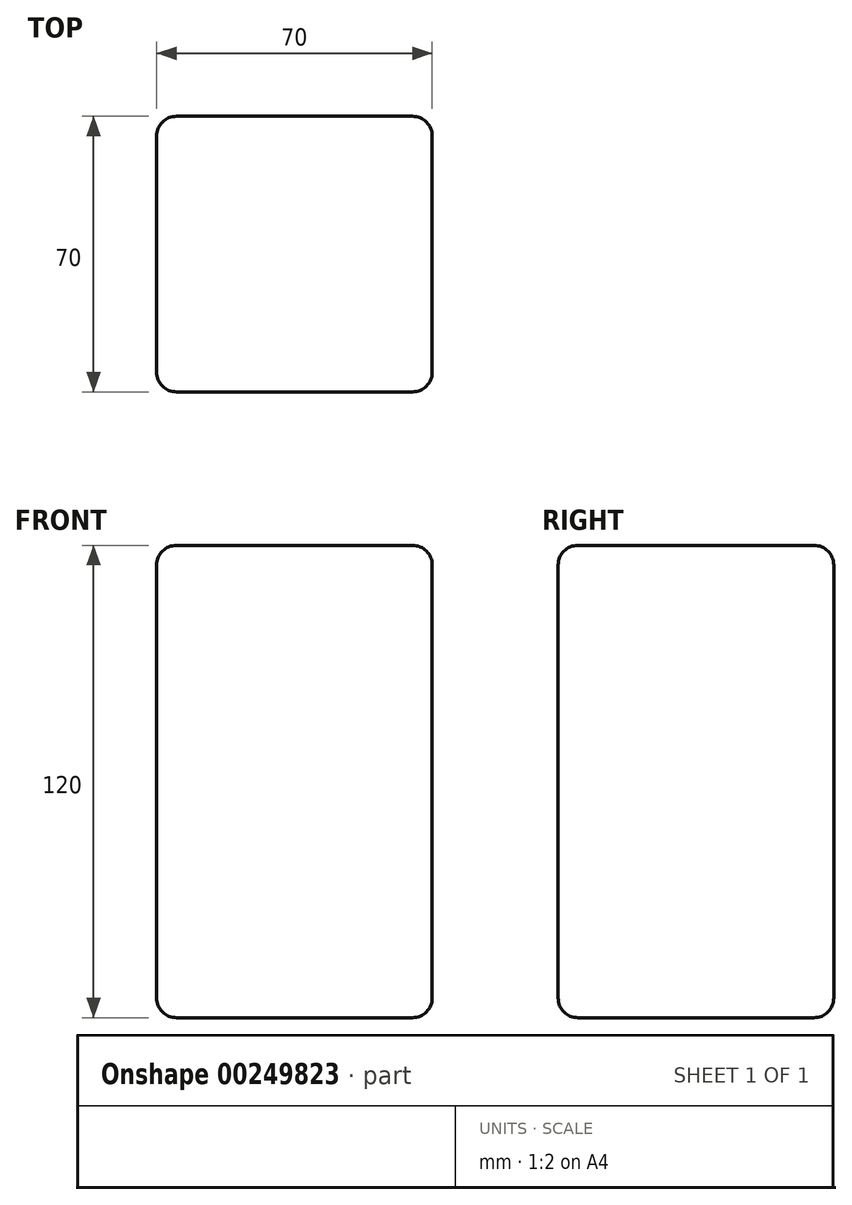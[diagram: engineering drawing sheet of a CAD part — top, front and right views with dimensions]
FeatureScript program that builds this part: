
annotation { "Feature Type Name" : "Feature", "Feature Type Description" : "" }
export const myFeature = defineFeature(function(context is Context, id is Id, definition is map)
    precondition{}
    {
        {
            var Q0;
            Q0=qCreatedBy(makeId("Top.planeOp"),FACE);
            var sketch = newSketch(context, id + "F0", { "sketchPlane" : qUnion([Q0])});
            skLineSegment(sketch, "E0.bottom", {"start": v(30, -34.82) * mm, "end": v(-30, -34.82) * mm});
            skLineSegment(sketch, "E0.top", {"start": v(30, 35.18) * mm, "end": v(-30, 35.18) * mm});
            skLineSegment(sketch, "E0.left", {"start": v(35, -29.82) * mm, "end": v(35, 30.18) * mm});
            skLineSegment(sketch, "E0.right", {"start": v(-35, -29.82) * mm, "end": v(-35, 30.18) * mm});
            skPoint(sketch, "E0.middle", {"position": v(0, 0.18) * mm});
            skPoint(sketch, "E1.visualSharp", {"position": v(-35, -34.82) * mm});
            skArc(sketch, "E1.filletArc", {"start": v(-35, -29.82) * mm, "mid": v(-33.54, -33.35) * mm, "end": v(-30, -34.82) * mm});
            skPoint(sketch, "E2.visualSharp", {"position": v(-35, 35.18) * mm});
            skArc(sketch, "E2.filletArc", {"start": v(-30, 35.18) * mm, "mid": v(-33.54, 33.72) * mm, "end": v(-35, 30.18) * mm});
            skPoint(sketch, "E3.visualSharp", {"position": v(35, 35.18) * mm});
            skArc(sketch, "E3.filletArc", {"start": v(35, 30.18) * mm, "mid": v(33.54, 33.72) * mm, "end": v(30, 35.18) * mm});
            skPoint(sketch, "E4.visualSharp", {"position": v(35, -34.82) * mm});
            skArc(sketch, "E4.filletArc", {"start": v(30, -34.82) * mm, "mid": v(33.54, -33.35) * mm, "end": v(35, -29.82) * mm});
            skSolve(sketch);
        }
        {
            var Q0;
            Q0=makeQuery(id+"F0.imprint","IMPRINT",FACE,{"disambiguationData":[TD([[makeQuery(id+"F0.imprint","IMPRINT",EDGE,{"derivedFrom":sQuery(id+"F0.wireOp",EDGE,"E0.bottom")}),-1.0]])]});
            extrude(context, id + "F1", {"entities" : qUnion([Q0]), "depth" : 120 * mm});
        }
        {
            var Q0;
            Q0=makeQuery(id+"F1.opExtrude","CAP_FACE",FACE,{"disambiguationData":[OSD([sQuery(id+"F0.wireOp",EDGE,"E0.bottom"),sQuery(id+"F0.wireOp",EDGE,"E0.top"),sQuery(id+"F0.wireOp",EDGE,"E0.left"),sQuery(id+"F0.wireOp",EDGE,"E0.right"),sQuery(id+"F0.wireOp",EDGE,"E1.filletArc"),sQuery(id+"F0.wireOp",EDGE,"E2.filletArc"),sQuery(id+"F0.wireOp",EDGE,"E3.filletArc"),sQuery(id+"F0.wireOp",EDGE,"E4.filletArc")])],"isStart":false});
            var Q1;
            Q1=makeQuery(id+"F1.opExtrude","CAP_FACE",FACE,{"disambiguationData":[OSD([sQuery(id+"F0.wireOp",EDGE,"E0.bottom"),sQuery(id+"F0.wireOp",EDGE,"E0.top"),sQuery(id+"F0.wireOp",EDGE,"E0.left"),sQuery(id+"F0.wireOp",EDGE,"E0.right"),sQuery(id+"F0.wireOp",EDGE,"E1.filletArc"),sQuery(id+"F0.wireOp",EDGE,"E2.filletArc"),sQuery(id+"F0.wireOp",EDGE,"E3.filletArc"),sQuery(id+"F0.wireOp",EDGE,"E4.filletArc")])],"isStart":true});
            fillet(context, id + "F2", {"entities" : qUnion([Q0, Q1]), "radius" : 5 * mm, "tangentPropagation" : true, "allowEdgeOverflow" : false});
        }
    });
